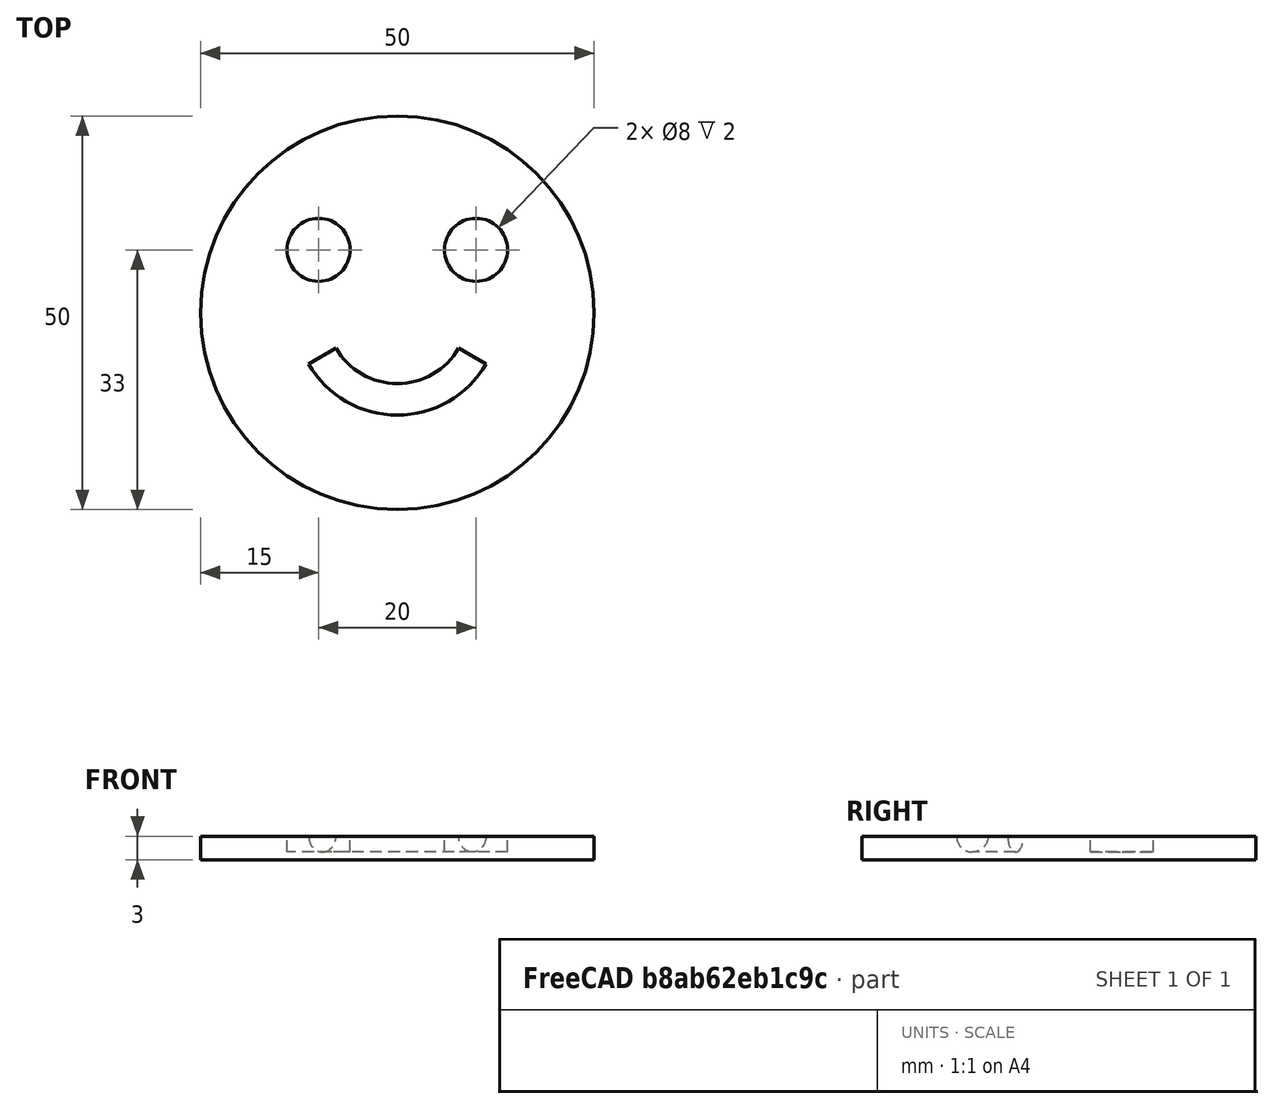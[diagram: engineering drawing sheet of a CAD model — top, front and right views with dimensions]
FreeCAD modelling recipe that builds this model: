
FCSTD DOCUMENT  (FreeCAD 0.18.4R)
Label: tutorial_freecad_ex15_b
License: All rights reserved
LicenseURL: http://en.wikipedia.org/wiki/All_rights_reserved
objects: Part::Cylinder×3, Part::Cut×2, Part::MultiFuse×1, Part::Torus×1
note: 7 computed .brp shape members not serialized (recipe doc carries the construction recipe); baked Part::Feature solids carry a one-line shape summary decoded from their .brp

FEATURE [Part::Cylinder] Cylinder  label="cabeza"
  Angle = 360
  AttacherType = Attacher::AttachEngine3D
  Height = 3
  Radius = 25
FEATURE [Part::Cylinder] Cylinder001  label="ojo_izq"
  Angle = 360
  AttacherType = Attacher::AttachEngine3D
  Height = 10
  Placement = pos=(-10,8,0) rot=(0,0,1;0rad)
  Radius = 4
FEATURE [Part::Cylinder] Cylinder002  label="ojo_der"
  Angle = 360
  AttacherType = Attacher::AttachEngine3D
  Height = 10
  Placement = pos=(10,8,0) rot=(0,0,1;0rad)
  Radius = 4
FEATURE [Part::MultiFuse] Fusion  label="ojos"
  Placement = pos=(0,0,1) rot=(0,0,1;0rad)
  Refine = true
  Shapes = -> [Cylinder001,Cylinder002]
FEATURE [Part::Cut] Cut  label="cabeza_con_ojos"
  Base = -> Cylinder
  Refine = true
  Tool = -> Fusion
FEATURE [Part::Torus] Torus  label="boca"
  Angle1 = -180
  Angle2 = 180
  Angle3 = 120
  AttacherType = Attacher::AttachEngine3D
  Placement = pos=(0,0,3) rot=(0,0,1;3.66519rad)
  Radius1 = 11
  Radius2 = 2
FEATURE [Part::Cut] Cut001  label="acid_house"
  Base = -> Cut
  Refine = true
  Tool = -> Torus
